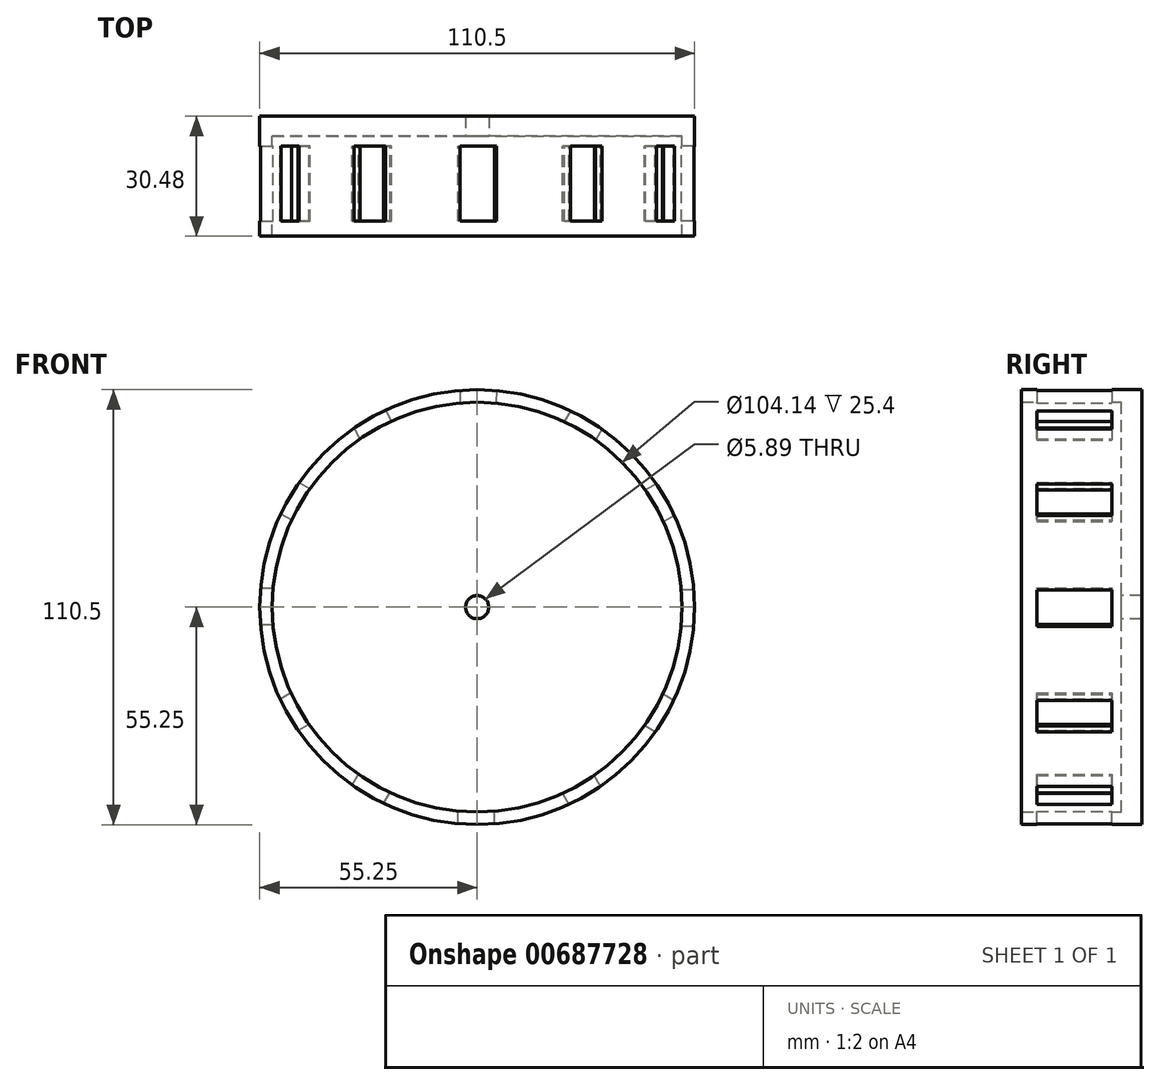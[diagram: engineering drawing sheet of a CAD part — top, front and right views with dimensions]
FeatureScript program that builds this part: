
annotation { "Feature Type Name" : "Feature", "Feature Type Description" : "" }
export const myFeature = defineFeature(function(context is Context, id is Id, definition is map)
    precondition{}
    {
        {
            var Q0;
            Q0=qCreatedBy(makeId("Front.planeOp"),FACE);
            var sketch = newSketch(context, id + "F0", { "sketchPlane" : qUnion([Q0])});
            skCircle(sketch, "E0", {"center": v(0, 0) * mm, "radius": 52.07 * mm});
            skCircle(sketch, "E1", {"center": v(0, 0) * mm, "radius": 55.24 * mm});
            skSolve(sketch);
        }
        {
            var Q0;
            Q0=makeQuery(id+"F0.imprint","IMPRINT",FACE,{"disambiguationData":[TD([[makeQuery(id+"F0.imprint","IMPRINT",EDGE,{"derivedFrom":sQuery(id+"F0.wireOp",EDGE,"E0")}),1.0]])]});
            extrude(context, id + "F1", {"entities" : qUnion([Q0]), "depth" : 5.08 * mm, "offsetDistance" : 25.4 * mm});
        }
        {
            var Q0;
            Q0=makeQuery(id+"F0.imprint","IMPRINT",FACE,{"disambiguationData":[TD([[makeQuery(id+"F0.imprint","IMPRINT",EDGE,{"derivedFrom":sQuery(id+"F0.wireOp",EDGE,"E0")}),-1.0]])]});
            extrude(context, id + "F2", {"entities" : qUnion([Q0]), "operationType" : NewBodyOperationType.ADD, "depth" : 30.48 * mm, "offsetDistance" : 25.4 * mm});
        }
        {
            var Q0;
            Q0=makeQuery(id+"F1.opExtrude","CAP_FACE",FACE,{"disambiguationData":[OSD([sQuery(id+"F0.wireOp",EDGE,"E0")])],"isStart":false});
            var sketch = newSketch(context, id + "F3", { "sketchPlane" : qUnion([Q0])});
            skCircle(sketch, "E2.cCircle", {"center": v(0, 0) * mm, "radius": 17.26 * mm, "construction": true});
            skLineSegment(sketch, "E2.0", {"start": v(12.58, -12.7) * mm, "end": v(4.55, -17.28) * mm});
            skLineSegment(sketch, "E2.1", {"start": v(4.55, -17.28) * mm, "end": v(-4.7, -17.24) * mm});
            skLineSegment(sketch, "E2.2", {"start": v(-4.7, -17.24) * mm, "end": v(-12.7, -12.58) * mm});
            skLineSegment(sketch, "E2.3", {"start": v(-12.7, -12.58) * mm, "end": v(-17.28, -4.55) * mm});
            skLineSegment(sketch, "E2.4", {"start": v(-17.28, -4.55) * mm, "end": v(-17.24, 4.7) * mm});
            skLineSegment(sketch, "E2.5", {"start": v(-17.24, 4.7) * mm, "end": v(-12.58, 12.7) * mm});
            skLineSegment(sketch, "E2.6", {"start": v(-12.58, 12.7) * mm, "end": v(-4.55, 17.28) * mm});
            skLineSegment(sketch, "E2.7", {"start": v(-4.55, 17.28) * mm, "end": v(4.7, 17.24) * mm});
            skLineSegment(sketch, "E2.8", {"start": v(4.7, 17.24) * mm, "end": v(12.7, 12.58) * mm});
            skLineSegment(sketch, "E2.9", {"start": v(12.7, 12.58) * mm, "end": v(17.28, 4.55) * mm});
            skLineSegment(sketch, "E2.10", {"start": v(17.28, 4.55) * mm, "end": v(17.24, -4.7) * mm});
            skLineSegment(sketch, "E2.11", {"start": v(17.24, -4.7) * mm, "end": v(12.58, -12.7) * mm});
            skPoint(sketch, "E2.0.midPoint", {"position": v(8.57, -14.99) * mm});
            skSolve(sketch);
        }
        {
            var Q0;
            Q0=makeQuery(id+"F3.imprint","IMPRINT",FACE,{"disambiguationData":[TD([[makeQuery(id+"F3.imprint","IMPRINT",EDGE,{"derivedFrom":sQuery(id+"F3.wireOp",EDGE,"E2.0")}),-1.0]])]});
            extrude(context, id + "F4", {"entities" : qUnion([Q0]), "operationType" : NewBodyOperationType.ADD, "depth" : 21.59 * mm, "offsetDistance" : 25.4 * mm});
        }
        {
            var Q0;
            Q0=makeQuery(id+"F4.opExtrude","SWEPT_FACE",FACE,{"disambiguationData":[OSD([sQuery(id+"F3.wireOp",EDGE,"E2.8")])]});
            var sketch = newSketch(context, id + "F5", { "sketchPlane" : qUnion([Q0])});
            skLineSegment(sketch, "E3", {"start": v(-4.63, -7.62) * mm, "end": v(4.63, -7.62) * mm});
            skSolve(sketch);
        }
        {
            var Q0;
            {var subQ0=sQuery(id+"F5.wireOp",EDGE,"E3");Q0=makeQuery(id+"F5.imprint","IMPRINT",FACE,{"disambiguationData":[TD([[makeQuery(id+"F5.imprint","IMPRINT",EDGE,{"derivedFrom":subQ0}),-1.0]])]});}
            extrude(context, id + "F6", {"entities" : qUnion([Q0]), "operationType" : NewBodyOperationType.REMOVE, "depth" : 50.8 * mm, "offsetDistance" : 25.4 * mm});
        }
        {
            var Q0;
            Q0=makeQuery(id+"F4.opExtrude","SWEPT_FACE",FACE,{"disambiguationData":[OSD([sQuery(id+"F3.wireOp",EDGE,"E2.7")])]});
            var sketch = newSketch(context, id + "F7", { "sketchPlane" : qUnion([Q0])});
            skLineSegment(sketch, "E4", {"start": v(4.63, -7.62) * mm, "end": v(-4.63, -7.62) * mm});
            skSolve(sketch);
        }
        {
            var Q0;
            {var subQ0=sQuery(id+"F7.wireOp",EDGE,"E4");Q0=makeQuery(id+"F7.imprint","IMPRINT",FACE,{"disambiguationData":[TD([[makeQuery(id+"F7.imprint","IMPRINT",EDGE,{"derivedFrom":subQ0}),1.0]])]});}
            extrude(context, id + "F8", {"entities" : qUnion([Q0]), "operationType" : NewBodyOperationType.REMOVE, "depth" : 50.8 * mm, "offsetDistance" : 25.4 * mm});
        }
        {
            var Q0;
            Q0=makeQuery(id+"F4.opExtrude","SWEPT_FACE",FACE,{"disambiguationData":[OSD([sQuery(id+"F3.wireOp",EDGE,"E2.6")])]});
            var sketch = newSketch(context, id + "F9", { "sketchPlane" : qUnion([Q0])});
            skLineSegment(sketch, "E5", {"start": v(4.63, -7.62) * mm, "end": v(-4.63, -7.62) * mm});
            skSolve(sketch);
        }
        {
            var Q0;
            {var subQ0=sQuery(id+"F9.wireOp",EDGE,"E5");Q0=makeQuery(id+"F9.imprint","IMPRINT",FACE,{"disambiguationData":[TD([[makeQuery(id+"F9.imprint","IMPRINT",EDGE,{"derivedFrom":subQ0}),1.0]])]});}
            extrude(context, id + "F10", {"entities" : qUnion([Q0]), "operationType" : NewBodyOperationType.REMOVE, "depth" : 50.8 * mm, "offsetDistance" : 25.4 * mm});
        }
        {
            var Q0;
            Q0=makeQuery(id+"F4.opExtrude","SWEPT_FACE",FACE,{"disambiguationData":[OSD([sQuery(id+"F3.wireOp",EDGE,"E2.5")])]});
            var sketch = newSketch(context, id + "F11", { "sketchPlane" : qUnion([Q0])});
            skLineSegment(sketch, "E6", {"start": v(7.62, 4.63) * mm, "end": v(7.62, -4.63) * mm});
            skSolve(sketch);
        }
        {
            var Q0;
            {var subQ0=sQuery(id+"F11.wireOp",EDGE,"E6");Q0=makeQuery(id+"F11.imprint","IMPRINT",FACE,{"disambiguationData":[TD([[makeQuery(id+"F11.imprint","IMPRINT",EDGE,{"derivedFrom":subQ0}),1.0]])]});}
            extrude(context, id + "F12", {"entities" : qUnion([Q0]), "operationType" : NewBodyOperationType.REMOVE, "depth" : 50.8 * mm, "offsetDistance" : 25.4 * mm});
        }
        {
            var Q0;
            Q0=makeQuery(id+"F4.opExtrude","SWEPT_FACE",FACE,{"disambiguationData":[OSD([sQuery(id+"F3.wireOp",EDGE,"E2.4")])]});
            var sketch = newSketch(context, id + "F13", { "sketchPlane" : qUnion([Q0])});
            skLineSegment(sketch, "E7", {"start": v(7.62, 4.63) * mm, "end": v(7.62, -4.63) * mm});
            skSolve(sketch);
        }
        {
            var Q0;
            {var subQ0=sQuery(id+"F13.wireOp",EDGE,"E7");Q0=makeQuery(id+"F13.imprint","IMPRINT",FACE,{"disambiguationData":[TD([[makeQuery(id+"F13.imprint","IMPRINT",EDGE,{"derivedFrom":subQ0}),1.0]])]});}
            extrude(context, id + "F14", {"entities" : qUnion([Q0]), "operationType" : NewBodyOperationType.REMOVE, "depth" : 50.8 * mm, "offsetDistance" : 25.4 * mm});
        }
        {
            var Q0;
            Q0=makeQuery(id+"F4.opExtrude","SWEPT_FACE",FACE,{"disambiguationData":[OSD([sQuery(id+"F3.wireOp",EDGE,"E2.3")])]});
            var sketch = newSketch(context, id + "F15", { "sketchPlane" : qUnion([Q0])});
            skLineSegment(sketch, "E8", {"start": v(7.62, 4.63) * mm, "end": v(7.62, -4.63) * mm});
            skSolve(sketch);
        }
        {
            var Q0;
            {var subQ0=sQuery(id+"F15.wireOp",EDGE,"E8");Q0=makeQuery(id+"F15.imprint","IMPRINT",FACE,{"disambiguationData":[TD([[makeQuery(id+"F15.imprint","IMPRINT",EDGE,{"derivedFrom":subQ0}),1.0]])]});}
            extrude(context, id + "F16", {"entities" : qUnion([Q0]), "operationType" : NewBodyOperationType.REMOVE, "depth" : 50.8 * mm, "offsetDistance" : 25.4 * mm});
        }
        {
            var Q0;
            Q0=makeQuery(id+"F4.opExtrude","SWEPT_FACE",FACE,{"disambiguationData":[OSD([sQuery(id+"F3.wireOp",EDGE,"E2.2")])]});
            var sketch = newSketch(context, id + "F17", { "sketchPlane" : qUnion([Q0])});
            skLineSegment(sketch, "E9", {"start": v(-4.63, 7.62) * mm, "end": v(4.63, 7.62) * mm});
            skSolve(sketch);
        }
        {
            var Q0;
            {var subQ0=sQuery(id+"F17.wireOp",EDGE,"E9");Q0=makeQuery(id+"F17.imprint","IMPRINT",FACE,{"disambiguationData":[TD([[makeQuery(id+"F17.imprint","IMPRINT",EDGE,{"derivedFrom":subQ0}),1.0]])]});}
            extrude(context, id + "F18", {"entities" : qUnion([Q0]), "operationType" : NewBodyOperationType.REMOVE, "depth" : 50.8 * mm, "offsetDistance" : 25.4 * mm});
        }
        {
            var Q0;
            Q0=makeQuery(id+"F4.opExtrude","SWEPT_FACE",FACE,{"disambiguationData":[OSD([sQuery(id+"F3.wireOp",EDGE,"E2.1")])]});
            var sketch = newSketch(context, id + "F19", { "sketchPlane" : qUnion([Q0])});
            skLineSegment(sketch, "E10", {"start": v(-4.63, 7.62) * mm, "end": v(4.63, 7.62) * mm});
            skSolve(sketch);
        }
        {
            var Q0;
            {var subQ0=sQuery(id+"F19.wireOp",EDGE,"E10");Q0=makeQuery(id+"F19.imprint","IMPRINT",FACE,{"disambiguationData":[TD([[makeQuery(id+"F19.imprint","IMPRINT",EDGE,{"derivedFrom":subQ0}),1.0]])]});}
            extrude(context, id + "F20", {"entities" : qUnion([Q0]), "operationType" : NewBodyOperationType.REMOVE, "depth" : 50.8 * mm, "offsetDistance" : 25.4 * mm});
        }
        {
            var Q0;
            Q0=makeQuery(id+"F4.opExtrude","SWEPT_FACE",FACE,{"disambiguationData":[OSD([sQuery(id+"F3.wireOp",EDGE,"E2.0")])]});
            var sketch = newSketch(context, id + "F21", { "sketchPlane" : qUnion([Q0])});
            skLineSegment(sketch, "E11", {"start": v(-4.63, 7.62) * mm, "end": v(4.63, 7.62) * mm});
            skSolve(sketch);
        }
        {
            var Q0;
            {var subQ0=sQuery(id+"F21.wireOp",EDGE,"E11");Q0=makeQuery(id+"F21.imprint","IMPRINT",FACE,{"disambiguationData":[TD([[makeQuery(id+"F21.imprint","IMPRINT",EDGE,{"derivedFrom":subQ0}),1.0]])]});}
            extrude(context, id + "F22", {"entities" : qUnion([Q0]), "operationType" : NewBodyOperationType.REMOVE, "depth" : 50.8 * mm, "offsetDistance" : 25.4 * mm});
        }
        {
            var Q0;
            Q0=makeQuery(id+"F4.opExtrude","SWEPT_FACE",FACE,{"disambiguationData":[OSD([sQuery(id+"F3.wireOp",EDGE,"E2.11")])]});
            var sketch = newSketch(context, id + "F23", { "sketchPlane" : qUnion([Q0])});
            skLineSegment(sketch, "E12", {"start": v(-7.62, -4.63) * mm, "end": v(-7.62, 4.63) * mm});
            skSolve(sketch);
        }
        {
            var Q0;
            {var subQ0=sQuery(id+"F23.wireOp",EDGE,"E12");Q0=makeQuery(id+"F23.imprint","IMPRINT",FACE,{"disambiguationData":[TD([[makeQuery(id+"F23.imprint","IMPRINT",EDGE,{"derivedFrom":subQ0}),1.0]])]});}
            extrude(context, id + "F24", {"entities" : qUnion([Q0]), "operationType" : NewBodyOperationType.REMOVE, "depth" : 50.8 * mm, "offsetDistance" : 25.4 * mm});
        }
        {
            var Q0;
            Q0=makeQuery(id+"F4.opExtrude","SWEPT_FACE",FACE,{"disambiguationData":[OSD([sQuery(id+"F3.wireOp",EDGE,"E2.10")])]});
            var sketch = newSketch(context, id + "F25", { "sketchPlane" : qUnion([Q0])});
            skLineSegment(sketch, "E13", {"start": v(-7.62, 4.63) * mm, "end": v(-7.62, -4.63) * mm});
            skSolve(sketch);
        }
        {
            var Q0;
            {var subQ0=sQuery(id+"F25.wireOp",EDGE,"E13");Q0=makeQuery(id+"F25.imprint","IMPRINT",FACE,{"disambiguationData":[TD([[makeQuery(id+"F25.imprint","IMPRINT",EDGE,{"derivedFrom":subQ0}),-1.0]])]});}
            extrude(context, id + "F26", {"entities" : qUnion([Q0]), "operationType" : NewBodyOperationType.REMOVE, "depth" : 50.8 * mm, "offsetDistance" : 25.4 * mm});
        }
        {
            var Q0;
            Q0=makeQuery(id+"F4.opExtrude","SWEPT_FACE",FACE,{"disambiguationData":[OSD([sQuery(id+"F3.wireOp",EDGE,"E2.9")])]});
            var sketch = newSketch(context, id + "F27", { "sketchPlane" : qUnion([Q0])});
            skLineSegment(sketch, "E14", {"start": v(-7.62, 4.63) * mm, "end": v(-7.62, -4.63) * mm});
            skSolve(sketch);
        }
        {
            var Q0;
            {var subQ0=sQuery(id+"F27.wireOp",EDGE,"E14");Q0=makeQuery(id+"F27.imprint","IMPRINT",FACE,{"disambiguationData":[TD([[makeQuery(id+"F27.imprint","IMPRINT",EDGE,{"derivedFrom":subQ0}),-1.0]])]});}
            extrude(context, id + "F28", {"entities" : qUnion([Q0]), "operationType" : NewBodyOperationType.REMOVE, "depth" : 50.8 * mm, "offsetDistance" : 25.4 * mm});
        }
        {
            var Q0;
            Q0=makeQuery(id+"F4.opExtrude","CAP_FACE",FACE,{"disambiguationData":[OSD([sQuery(id+"F3.wireOp",EDGE,"E2.0"),sQuery(id+"F3.wireOp",EDGE,"E2.1"),sQuery(id+"F3.wireOp",EDGE,"E2.2"),sQuery(id+"F3.wireOp",EDGE,"E2.3"),sQuery(id+"F3.wireOp",EDGE,"E2.4"),sQuery(id+"F3.wireOp",EDGE,"E2.5"),sQuery(id+"F3.wireOp",EDGE,"E2.6"),sQuery(id+"F3.wireOp",EDGE,"E2.7"),sQuery(id+"F3.wireOp",EDGE,"E2.8"),sQuery(id+"F3.wireOp",EDGE,"E2.9"),sQuery(id+"F3.wireOp",EDGE,"E2.10"),sQuery(id+"F3.wireOp",EDGE,"E2.11")])],"isStart":false});
            extrude(context, id + "F29", {"entities" : qUnion([Q0]), "operationType" : NewBodyOperationType.REMOVE, "oppositeDirection" : true, "depth" : 21.59 * mm, "offsetDistance" : 25.4 * mm});
        }
        {
            var Q0;
            Q0=makeQuery(id+"F29.boolean.opBoolean","MERGE",FACE,{"derivedFrom":[makeQuery(id+"F1.opExtrude","CAP_FACE",FACE,{"disambiguationData":[OSD([sQuery(id+"F0.wireOp",EDGE,"E0")])],"isStart":false}),makeQuery(id+"F29.opExtrude","CAP_FACE",FACE,{"disambiguationData":[OSD([sQuery(id+"F3.wireOp",EDGE,"E2.0"),sQuery(id+"F3.wireOp",EDGE,"E2.1"),sQuery(id+"F3.wireOp",EDGE,"E2.2"),sQuery(id+"F3.wireOp",EDGE,"E2.3"),sQuery(id+"F3.wireOp",EDGE,"E2.4"),sQuery(id+"F3.wireOp",EDGE,"E2.5"),sQuery(id+"F3.wireOp",EDGE,"E2.6"),sQuery(id+"F3.wireOp",EDGE,"E2.7"),sQuery(id+"F3.wireOp",EDGE,"E2.8"),sQuery(id+"F3.wireOp",EDGE,"E2.9"),sQuery(id+"F3.wireOp",EDGE,"E2.10"),sQuery(id+"F3.wireOp",EDGE,"E2.11")])],"isStart":false})]});
            var sketch = newSketch(context, id + "F30", { "sketchPlane" : qUnion([Q0])});
            skCircle(sketch, "E15", {"center": v(0, 0) * mm, "radius": 2.95 * mm});
            skSolve(sketch);
        }
        {
            var Q0;
            Q0=makeQuery(id+"F30.imprint","IMPRINT",FACE,{"disambiguationData":[TD([[makeQuery(id+"F30.imprint","IMPRINT",EDGE,{"derivedFrom":sQuery(id+"F30.wireOp",EDGE,"E15")}),1.0]])]});
            extrude(context, id + "F31", {"entities" : qUnion([Q0]), "operationType" : NewBodyOperationType.REMOVE, "oppositeDirection" : true, "depth" : 8.38 * mm, "offsetDistance" : 25.4 * mm});
        }
    });
